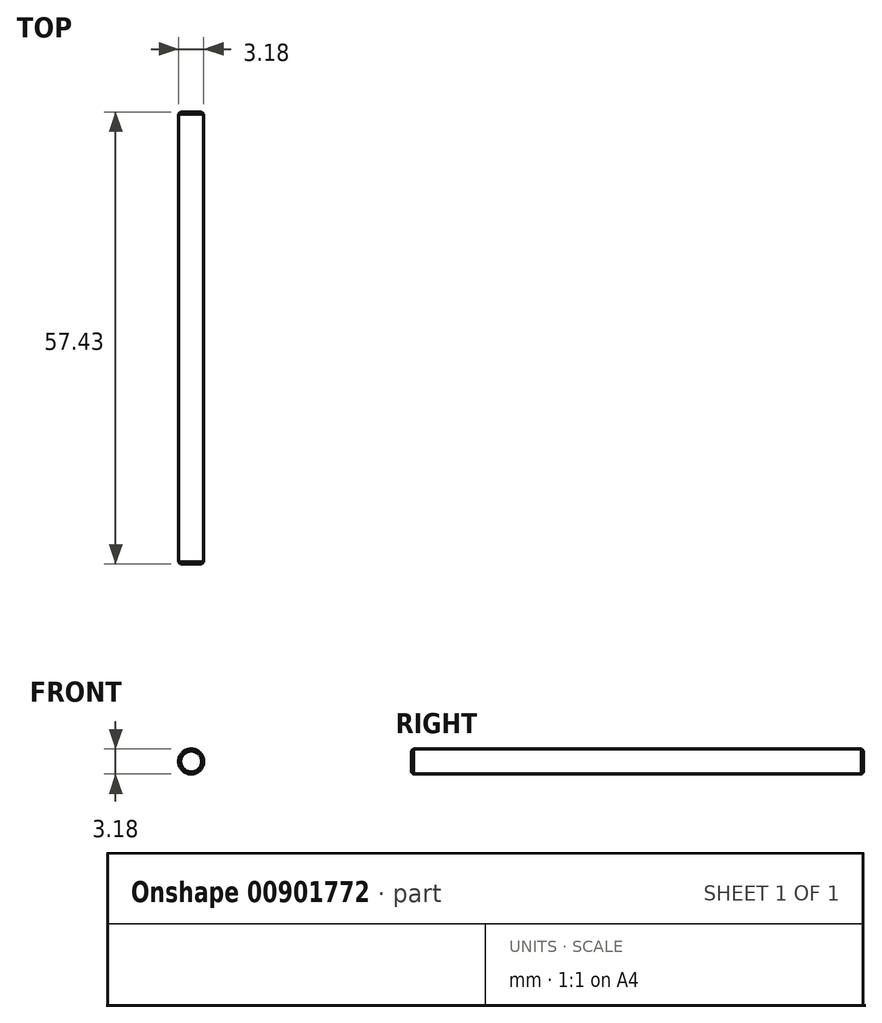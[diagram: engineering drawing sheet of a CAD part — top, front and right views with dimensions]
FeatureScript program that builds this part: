
annotation { "Feature Type Name" : "Feature", "Feature Type Description" : "" }
export const myFeature = defineFeature(function(context is Context, id is Id, definition is map)
    precondition{}
    {
        {
            var Q0;
            Q0=qCreatedBy(makeId("Front.planeOp"),FACE);
            var sketch = newSketch(context, id + "F0", { "sketchPlane" : qUnion([Q0])});
            skCircle(sketch, "E0", {"center": v(0, 0) * mm, "radius": 1.59 * mm});
            skSolve(sketch);
        }
        {
            var Q0;
            Q0=makeQuery(id+"F0.imprint","IMPRINT",FACE,{"disambiguationData":[TD([[makeQuery(id+"F0.imprint","IMPRINT",EDGE,{"derivedFrom":sQuery(id+"F0.wireOp",EDGE,"E0")}),1.0]])]});
            var Q1;
            Q1=sQuery(id+"F0.wireOp",EDGE,"E0");
            extrude(context, id + "F1", {"entities" : qUnion([Q0]), "surfaceEntities" : qUnion([Q1]), "depth" : 57.43 * mm, "offsetDistance" : 25 * mm});
        }
        {
            var Q0;
            Q0=makeQuery(id+"F1.opExtrude","CAP_EDGE",EDGE,{"disambiguationData":[OSD([sQuery(id+"F0.wireOp",EDGE,"E0")])],"isStart":false});
            var Q1;
            Q1=makeQuery(id+"F1.opExtrude","CAP_EDGE",EDGE,{"disambiguationData":[OSD([sQuery(id+"F0.wireOp",EDGE,"E0")])],"isStart":true});
            chamfer(context, id + "F2", {"entities" : qUnion([Q0, Q1]), "width" : 0.25 * mm, "tangentPropagation" : true});
        }
    });
